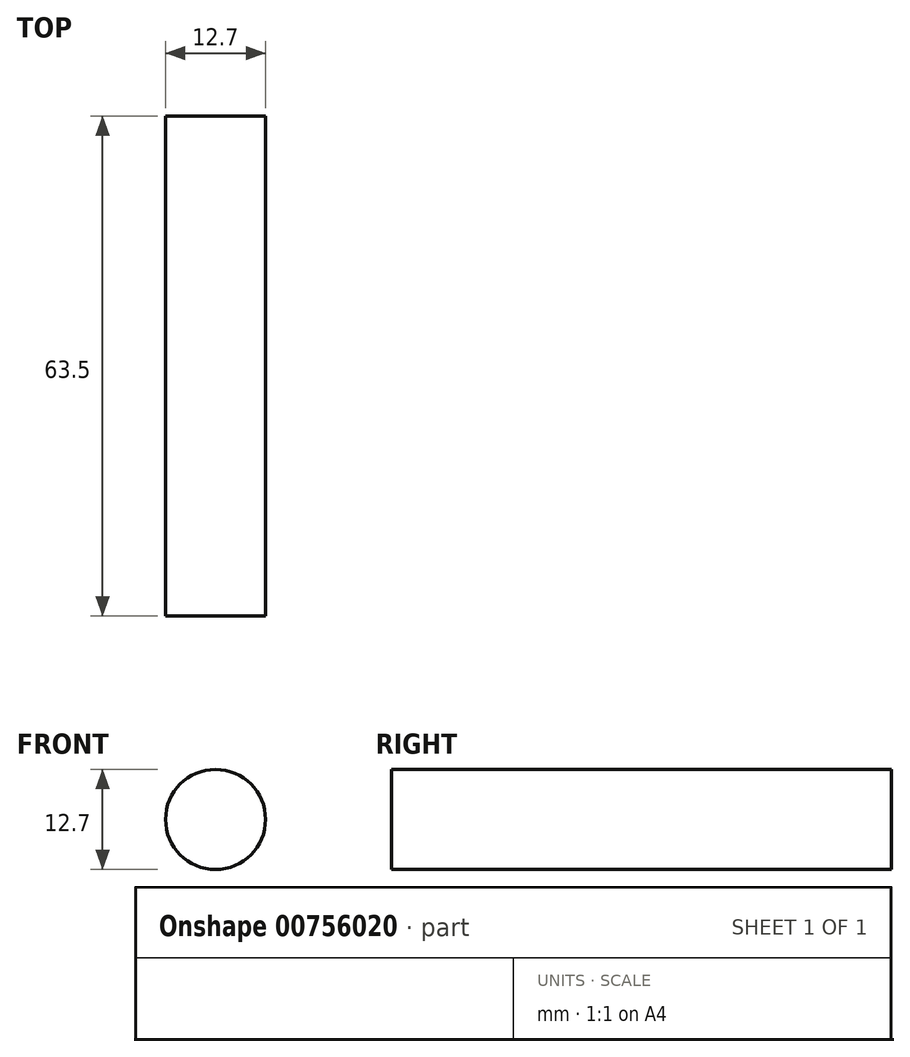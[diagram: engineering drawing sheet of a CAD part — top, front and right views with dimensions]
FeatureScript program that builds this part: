
annotation { "Feature Type Name" : "Feature", "Feature Type Description" : "" }
export const myFeature = defineFeature(function(context is Context, id is Id, definition is map)
    precondition{}
    {
        {
            var Q0;
            Q0=qCreatedBy(makeId("Front.planeOp"),FACE);
            var sketch = newSketch(context, id + "F0", { "sketchPlane" : qUnion([Q0])});
            skCircle(sketch, "E0", {"center": v(0, 0) * mm, "radius": 6.35 * mm});
            skSolve(sketch);
        }
        {
            var Q0;
            Q0=makeQuery(id+"F0.imprint","IMPRINT",FACE,{"disambiguationData":[TD([[makeQuery(id+"F0.imprint","IMPRINT",EDGE,{"derivedFrom":sQuery(id+"F0.wireOp",EDGE,"E0")}),1.0]])]});
            extrude(context, id + "F1", {"entities" : qUnion([Q0]), "depth" : 63.5 * mm, "offsetDistance" : 25.4 * mm});
        }
    });
